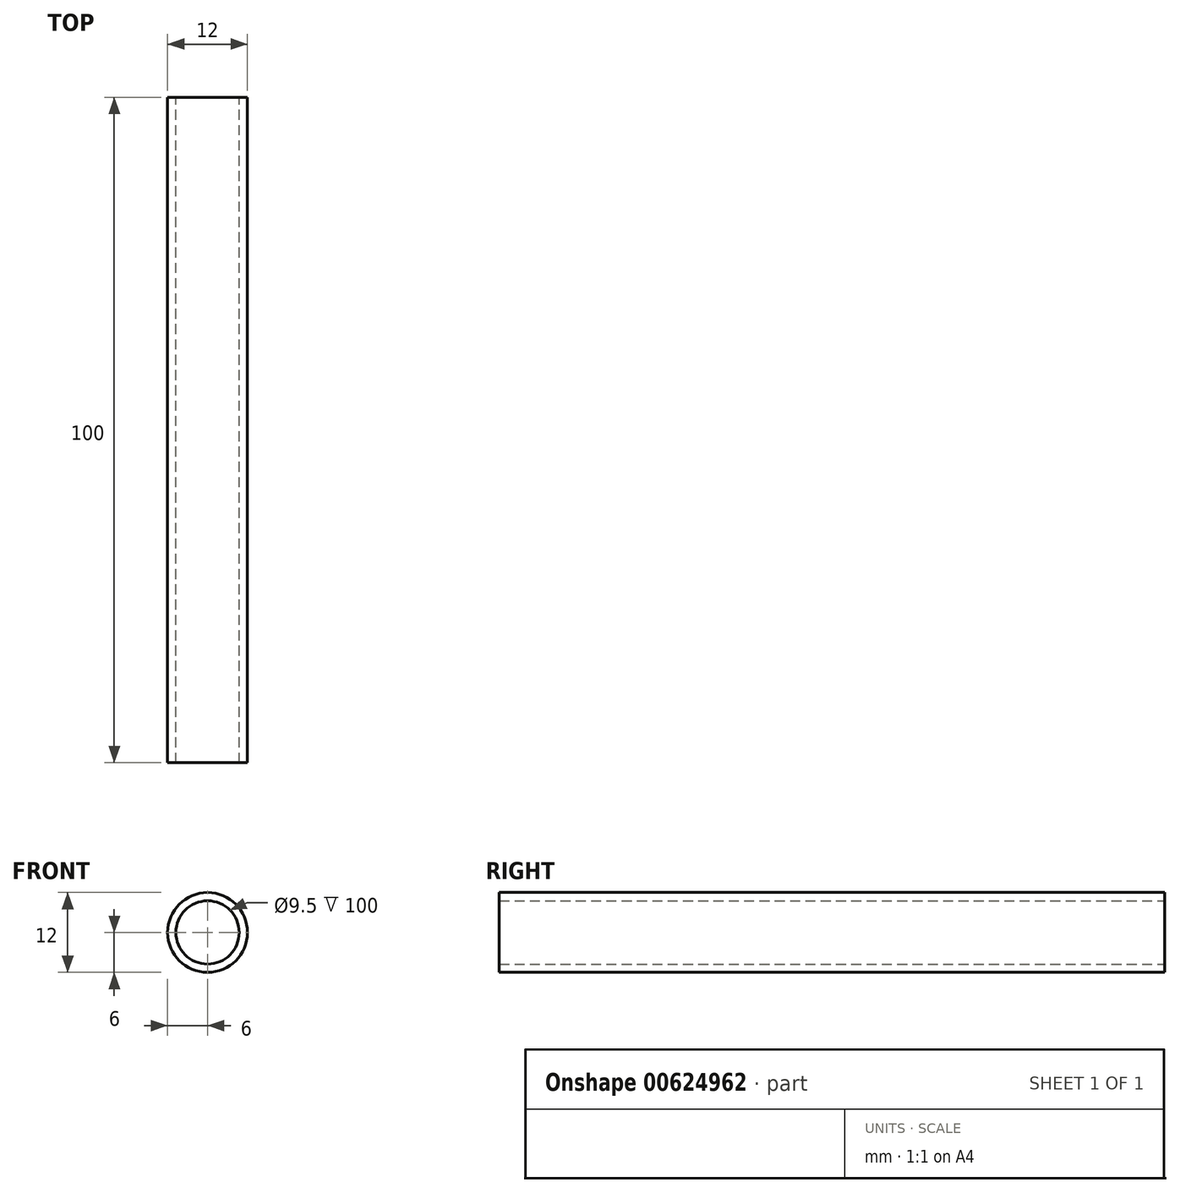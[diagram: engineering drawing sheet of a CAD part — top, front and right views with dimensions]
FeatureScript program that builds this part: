
annotation { "Feature Type Name" : "Feature", "Feature Type Description" : "" }
export const myFeature = defineFeature(function(context is Context, id is Id, definition is map)
    precondition{}
    {
        {
            var Q0;
            Q0=qCreatedBy(makeId("Front.planeOp"),FACE);
            var sketch = newSketch(context, id + "F0", { "sketchPlane" : qUnion([Q0])});
            skCircle(sketch, "E0", {"center": v(0, 0) * mm, "radius": 6 * mm});
            skCircle(sketch, "E1", {"center": v(0, 0) * mm, "radius": 4.75 * mm});
            skSolve(sketch);
        }
        {
            var Q0;
            Q0=makeQuery(id+"F0.imprint","IMPRINT",FACE,{"disambiguationData":[TD([[makeQuery(id+"F0.imprint","IMPRINT",EDGE,{"derivedFrom":sQuery(id+"F0.wireOp",EDGE,"E0")}),1.0]])]});
            extrude(context, id + "F1", {"entities" : qUnion([Q0]), "endBound" : BoundingType.SYMMETRIC, "depth" : 100 * mm, "offsetDistance" : 25 * mm});
        }
    });
